# Revit family: LAMP_OCULT RECESSED PROFILE
name_source: partatom
category: Luminarias
revit_build: Autodesk Revit 2015 (Build: 20140606_1530(x64)
units: mm (PartAtom-declared; Revit-internal decimal feet)

## types (32) — shared parameters
Comentarios de tipo = Availability of changing profile version and height when placed in project.
Elevación por defecto = 1219 mm
Fabricante = LAMP
IEE = A+
Installation instructions = https://www.lamp.es
Insulation class = I
Last update = 30/07/2019
Luminaire type = Profile
Manufacturer URL = http://www.lamp.es
Manufacturer country = Spain
Manufacturer name = LAMP
Material suspension = Panel de metal
Model explanation = Availability of changing profile version and height when placed in project.
Product URL = https://www.lamp.es
Product datasheet = http://www.lamp.es
Protection rating = IP20

## per-type parameters (varying)
| type | Descripción | Dimensions | Finish | Length | Material perfil | Modelo | Product code | Recessed dimensions | Weight |
| 500mm Recessed  BLACK | OCULT SYS. ACC. REC PROFILE 500 WH. | 500x53x96 | Matte white RAL 9010 | 500 mm  [stored 1.64042 ft] | LAMP_Aluminio Ocult Pendular NG | OSREPR500W | OSREPR500W | 510x59 | 1.23 kg |
| 500mm Recessed  WHITE | OCULT SYS. ACC. SUR PROFILE 500 BK. | 500x53x96 | Matte black RAL 9011 | 500 mm  [stored 1.64042 ft] | LAMP_Aluminio Ocult Pendular BL | OSSUPR500B | OSSUPR500B | 510x59 | 0.84 kg |
| 600mm Recessed  BLACK | OCULT SYS. ACC. REC PROFILE 600 BK. | 600x53x96 | Matte black RAL 9011 | 600 mm | LAMP_Aluminio Ocult Pendular NG | OSREPR600B | OSREPR600B | 610x59 | 1.43 kg |
| 600mm Recessed  WHITE | OCULT SYS. ACC. REC PROFILE 600 WH. | 600x53x96 | Matte white RAL 9010 | 600 mm | LAMP_Aluminio Ocult Pendular BL | OSREPR600W | OSREPR600W | 610x59 | 1.43 kg |
| 700mm Recessed  BLACK | OCULT SYS. ACC. REC PROFILE 700 BK. | 700x53x96 | Matte black RAL 9011 | 700 mm  [stored 2.29659 ft] | LAMP_Aluminio Ocult Pendular NG | OSREPR700B | OSREPR700B | 710x59 | 1.75 kg |
| 700mm Recessed  WHITE | OCULT SYS. ACC. REC PROFILE 700 WH. | 700x53x96 | Matte white RAL 9010 | 700 mm  [stored 2.29659 ft] | LAMP_Aluminio Ocult Pendular BL | OSREPR700W | OSREPR700W | 710x59 | 1.75 kg |
| 800mm Recessed  BLACK | OCULT SYS. ACC. REC PROFILE 800 BK. | 800x53x96 | Matte black RAL 9011 | 800 mm  [stored 2.62467 ft] | LAMP_Aluminio Ocult Pendular NG | OSREPR800B | OSREPR800B | 810x59 | 1.95 kg |
| 800mm Recessed  WHITE | OCULT SYS. ACC. REC PROFILE 800 WH. | 800x53x96 | Matte white RAL 9010 | 800 mm  [stored 2.62467 ft] | LAMP_Aluminio Ocult Pendular BL | OSREPR800W | OSREPR800W | 810x59 | 1.95 kg |
| 900mm Recessed  BLACK | OCULT SYS. ACC. REC PROFILE 900 BK. | 900x53x96 | Matte black RAL 9011 | 900 mm  [stored 2.95276 ft] | LAMP_Aluminio Ocult Pendular NG | OSREPR900B | OSREPR900B | 910x59 | 2.14 kg |
| 900mm Recessed  WHITE | OCULT SYS. ACC. REC PROFILE 900 WH. | 900x53x96 | Matte white RAL 9010 | 900 mm  [stored 2.95276 ft] | LAMP_Aluminio Ocult Pendular BL | OSREPR900W | OSREPR900W | 910x59 | 2.14 kg |
| 1000mm Recessed  BLACK | OCULT SYS. ACC. REC PROFILE 1000 BK. | 1000x53x96 | Matte black RAL 9011 | 1000 mm  [stored 3.28084 ft] | LAMP_Aluminio Ocult Pendular NG | OSREPR1000B | OSREPR1000B | 1010x59 | 2.33 kg |
| 1000mm Recessed  WHITE | OCULT SYS. ACC. REC PROFILE 1000 WH. | 1000x53x96 | Matte white RAL 9010 | 1000 mm  [stored 3.28084 ft] | LAMP_Aluminio Ocult Pendular BL | OSREPR1000W | OSREPR1000W | 1010x59 | 2.33 kg |
| 1100mm Recessed  BLACK | OCULT SYS. ACC. REC PROFILE 1100 BK. | 1100x53x96 | Matte black RAL 9011 | 1100 mm | LAMP_Aluminio Ocult Pendular NG | OSREPR1100B | OSREPR1100B | 1110x59 | 2.53 kg |
| 1100mm Recessed  WHITE | OCULT SYS. ACC. REC PROFILE 1100 WH. | 1100x53x96 | Matte white RAL 9010 | 1100 mm | LAMP_Aluminio Ocult Pendular BL | OSREPR1100W | OSREPR1100W | 1110x59 | 2.53 kg |
| 1200mm Recessed  BLACK | OCULT SYS. ACC. REC PROFILE 1200 BK. | 1200x53x96 | Matte black RAL 9011 | 1200 mm | LAMP_Aluminio Ocult Pendular NG | OSREPR1200B | OSREPR1200B | 1210x59 | 2.85 kg |
| 1200mm Recessed  WHITE | OCULT SYS. ACC. REC PROFILE 1200 WH. | 1200x53x96 | Matte white RAL 9010 | 1200 mm | LAMP_Aluminio Ocult Pendular BL | OSREPR1200W | OSREPR1200W | 1210x59 | 2.85 kg |
| 1300mm Recessed  BLACK | OCULT SYS. ACC. REC PROFILE 1300 BK. | 1300x53x96 | Matte black RAL 9011 | 1300 mm  [stored 4.26509 ft] | LAMP_Aluminio Ocult Pendular NG | OSREPR1300B | OSREPR1300B | 1310x59 | 3.05 kg |
| 1300mm Recessed  WHITE | OCULT SYS. ACC. REC PROFILE 1300 WH. | 1300x53x96 | Matte white RAL 9010 | 1300 mm  [stored 4.26509 ft] | LAMP_Aluminio Ocult Pendular BL | OSREPR1300W | OSREPR1300W | 1310x59 | 3.05 kg |
| 1400mm Recessed  BLACK | OCULT SYS. ACC. REC PROFILE 1400 BK. | 1400x53x96 | Matte black RAL 9011 | 1400 mm  [stored 4.59318 ft] | LAMP_Aluminio Ocult Pendular NG | OSREPR1400B | OSREPR1400B | 1410x59 | 3.24 kg |
| 1400mm Recessed  WHITE | OCULT SYS. ACC. REC PROFILE 1400 WH. | 1400x53x96 | Matte white RAL 9010 | 1400 mm  [stored 4.59318 ft] | LAMP_Aluminio Ocult Pendular BL | OSREPR1400W | OSREPR1400W | 1410x59 | 3.24 kg |
| 1500mm Recessed  BLACK | OCULT SYS. ACC. REC PROFILE 1500 BK. | 1500x53x96 | Matte black RAL 9011 | 1500 mm  [stored 4.92126 ft] | LAMP_Aluminio Ocult Pendular NG | OSREPR1500B | OSREPR1500B | 1510x59 | 3.44 kg |
| 1500mm Recessed  WHITE | OCULT SYS. ACC. REC PROFILE 1500 WH. | 1500x53x96 | Matte white RAL 9010 | 1500 mm  [stored 4.92126 ft] | LAMP_Aluminio Ocult Pendular BL | OSREPR1500W | OSREPR1500W | 1510x59 | 3.44 kg |
| 1600mm Recessed  BLACK | OCULT SYS. ACC. REC PROFILE 1600 BK. | 1600x53x96 | Matte black RAL 9011 | 1600 mm  [stored 5.24934 ft] | LAMP_Aluminio Ocult Pendular NG | OSREPR1600B | OSREPR1600B | 1610x59 | 3.63 kg |
| 1600mm Recessed  WHITE | OCULT SYS. ACC. REC PROFILE 1600 WH. | 1600x53x96 | Matte white RAL 9010 | 1600 mm  [stored 5.24934 ft] | LAMP_Aluminio Ocult Pendular BL | OSREPR1600W | OSREPR1600W | 1610x59 | 3.63 kg |
| 1700mm Recessed  BLACK | OCULT SYS. ACC. REC PROFILE 1700 BK. | 1700x53x96 | Matte black RAL 9011 | 1700 mm  [stored 5.57743 ft] | LAMP_Aluminio Ocult Pendular NG | OSREPR1700B | OSREPR1700B | 1710x59 | 3.82 kg |
| 1700mm Recessed  WHITE | OCULT SYS. ACC. REC PROFILE 1700 WH. | 1700x53x96 | Matte white RAL 9010 | 1700 mm  [stored 5.57743 ft] | LAMP_Aluminio Ocult Pendular BL | OSREPR1700W | OSREPR1700W | 1710x59 | 3.82 kg |
| 1800mm Recessed  BLACK | OCULT SYS. ACC. REC PROFILE 1800 BK. | 1800x53x96 | Matte black RAL 9011 | 1800 mm  [stored 5.90551 ft] | LAMP_Aluminio Ocult Pendular NG | OSREPR1800B | OSREPR1800B | 1810x59 | 4.15 kg |
| 1800mm Recessed  WHITE | OCULT SYS. ACC. REC PROFILE 1800 WH. | 1800x53x96 | Matte white RAL 9010 | 1800 mm  [stored 5.90551 ft] | LAMP_Aluminio Ocult Pendular BL | OSREPR1800W | OSREPR1800W | 1810x59 | 4.15 kg |
| 1900mm Recessed  BLACK | OCULT SYS. ACC. REC PROFILE 1900 BK. | 1900x53x96 | Matte black RAL 9011 | 1900 mm  [stored 6.2336 ft] | LAMP_Aluminio Ocult Pendular NG | OSREPR1900B | OSREPR1900B | 1910x59 | 4.34 kg |
| 1900mm Recessed  WHITE | OCULT SYS. ACC. REC PROFILE 1900 WH. | 1900x53x96 | Matte white RAL 9010 | 1900 mm  [stored 6.2336 ft] | LAMP_Aluminio Ocult Pendular BL | OSREPR1900W | OSREPR1900W | 1910x59 | 4.34 kg |
| 2000mm Recessed  BLACK | OCULT SYS. ACC. REC PROFILE 2000 BK. | 2000x53x96 | Matte black RAL 9011 | 2000 mm  [stored 6.56168 ft] | LAMP_Aluminio Ocult Pendular NG | OSREPR2000B | OSREPR2000B | 2021x59 | 4.54 kg |
| 2000mm Recessed  WHITE | OCULT SYS. ACC. REC PROFILE 2000 WH. | 2000x53x96 | Matte white RAL 9010 | 2000 mm  [stored 6.56168 ft] | LAMP_Aluminio Ocult Pendular BL | OSREPR2000W | OSREPR2000W | 2021x59 | 4.54 kg |

note: [stored X ft] marks values corroborated as IEEE doubles in the binary element streams (Revit-internal decimal feet)
